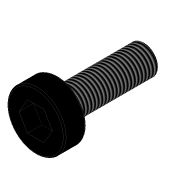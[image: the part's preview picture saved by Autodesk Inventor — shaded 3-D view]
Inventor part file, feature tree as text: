
AUTODESK INVENTOR PART (.ipt)
format: ipt  version: 2020 (Build 240168000, 168)  size: 129,024 bytes
history: native  units: mm
features: extrude x3, sketch x3, fillet x1, thread x1
ambient origin geometry x8: Origin, YZ Plane, XZ Plane, XY Plane, X Axis, Y Axis, Z Axis, Center Point
bodies: Solid1 (feature_tree)
feature tree (8):
  extrude  "Extrusion1"  Depth=4.0mm
  extrude  "Extrusion2"  Depth=1.0mm TaperAngle=0.0deg
  extrude  "Extrusion3"  Depth=12.0mm TaperAngle=0.0deg
  fillet  "Fillet1"  Radius=0.2mm
  thread  "Thread1"  [1 undecoded]
  sketch  "Sketch1"  dims[d0=8.0mm d1=4.0mm]
  sketch  "Sketch2"  dims[d2=2.0mm d3=0.0mm d4=1.0mm d5=0.0mm]
  sketch  "Sketch3"  dims[d6=4.0mm d7=12.0mm d8=0.0mm d9=0.2mm d10=7.3mm d11=0.0mm]
note: 1 required parameter value undecoded (feature->parameter linkage not recoverable at this tier; creation-order binding heuristic only, values carry confidence <= 0.55)
